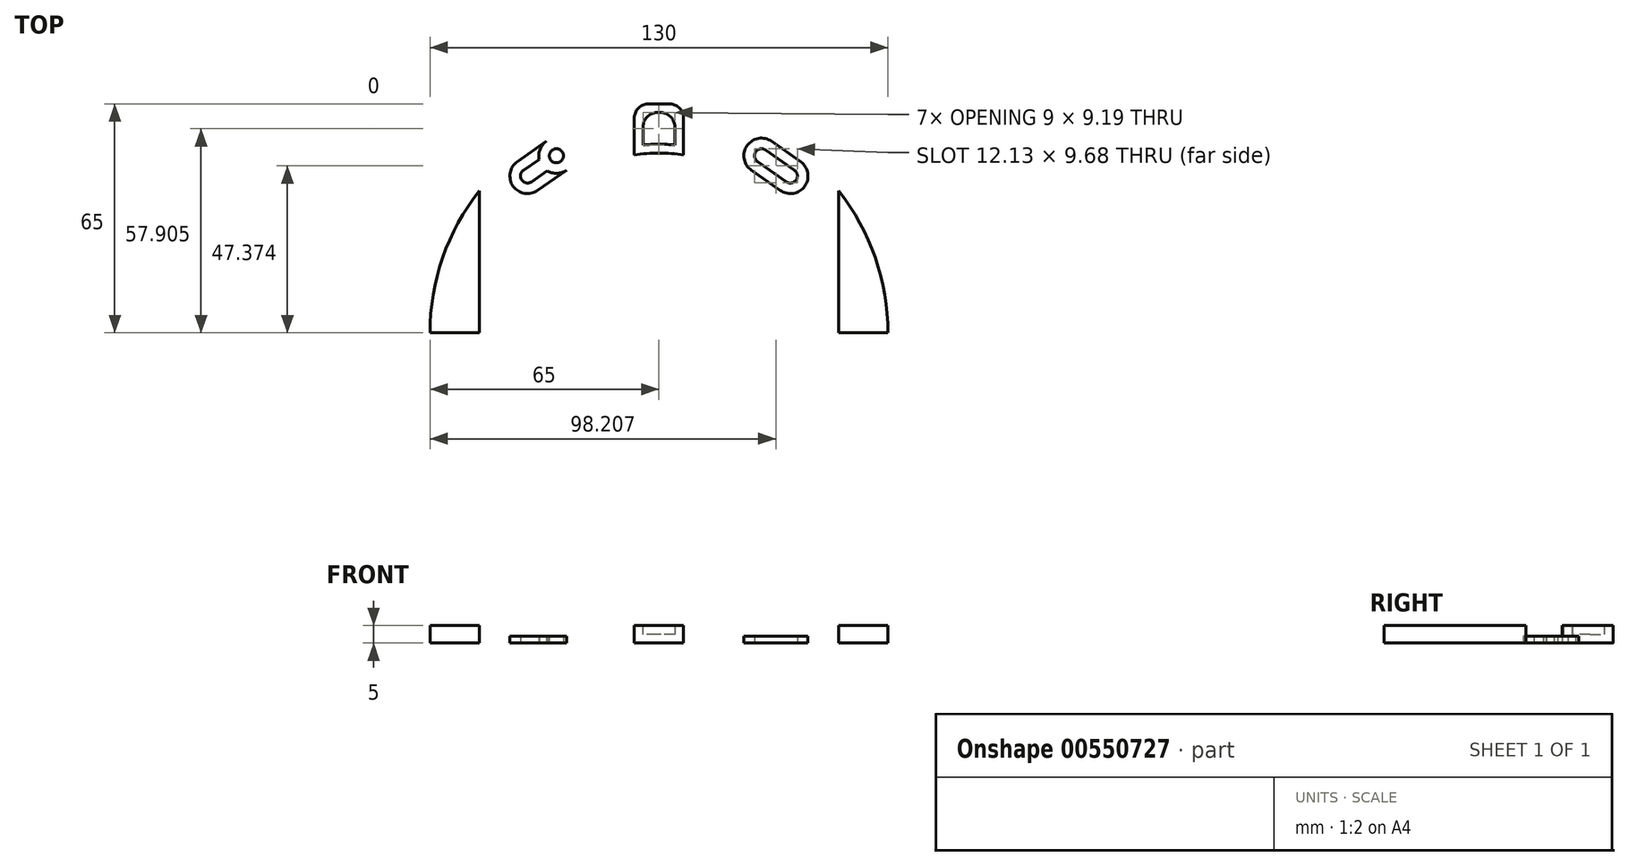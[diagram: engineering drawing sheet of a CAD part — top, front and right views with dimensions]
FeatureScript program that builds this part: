
annotation { "Feature Type Name" : "Feature", "Feature Type Description" : "" }
export const myFeature = defineFeature(function(context is Context, id is Id, definition is map)
    precondition{}
    {
        {
            var Q0;
            Q0=qCreatedBy(makeId("Top.planeOp"),FACE);
            var sketch = newSketch(context, id + "F0", { "sketchPlane" : qUnion([Q0])});
            skLineSegment(sketch, "E0.rect.bottom", {"start": v(-120.25, 41.25) * mm, "end": v(120.25, 41.25) * mm});
            skLineSegment(sketch, "E0.rect.top", {"start": v(-120.25, -41.25) * mm, "end": v(120.25, -41.25) * mm});
            skLineSegment(sketch, "E0.rect.left", {"start": v(-120.25, 41.25) * mm, "end": v(-120.25, -41.25) * mm});
            skLineSegment(sketch, "E0.rect.right", {"start": v(120.25, 41.25) * mm, "end": v(120.25, -41.25) * mm});
            skPoint(sketch, "E0.rect.middle", {"position": v(0, 0) * mm});
            skLineSegment(sketch, "E1.rect.bottom", {"start": v(-65, 41.25) * mm, "end": v(65, 41.25) * mm});
            skLineSegment(sketch, "E1.rect.top", {"start": v(-65, -41.25) * mm, "end": v(65, -41.25) * mm});
            skLineSegment(sketch, "E1.rect.left", {"start": v(-65, 41.25) * mm, "end": v(-65, -41.25) * mm});
            skLineSegment(sketch, "E1.rect.right", {"start": v(65, 41.25) * mm, "end": v(65, -41.25) * mm});
            skArc(sketch, "E2", {"start": v(65, -41.25) * mm, "mid": v(0, 23.75) * mm, "end": v(-65, -41.25) * mm});
            skLineSegment(sketch, "E3.rect.bottom", {"start": v(-51, 41.25) * mm, "end": v(51, 41.25) * mm});
            skLineSegment(sketch, "E3.rect.top", {"start": v(-51, -41.25) * mm, "end": v(51, -41.25) * mm});
            skLineSegment(sketch, "E3.rect.left", {"start": v(-51, 41.25) * mm, "end": v(-51, -41.25) * mm});
            skLineSegment(sketch, "E3.rect.right", {"start": v(51, 41.25) * mm, "end": v(51, -41.25) * mm});
            skArc(sketch, "E4", {"start": v(51, -41.25) * mm, "mid": v(0, 9.75) * mm, "end": v(-51, -41.25) * mm});
            skLineSegment(sketch, "E5.rect.bottom", {"start": v(-7, 41.25) * mm, "end": v(7, 41.25) * mm});
            skLineSegment(sketch, "E5.rect.top", {"start": v(-7, -41.25) * mm, "end": v(7, -41.25) * mm});
            skLineSegment(sketch, "E5.rect.left", {"start": v(-7, 41.25) * mm, "end": v(-7, -41.25) * mm});
            skLineSegment(sketch, "E5.rect.right", {"start": v(7, 41.25) * mm, "end": v(7, -41.25) * mm});
            skLineSegment(sketch, "E6", {"start": v(7, -41.25) * mm, "end": v(51, 41.25) * mm, "construction": true});
            skLineSegment(sketch, "E7", {"start": v(0, -41.25) * mm, "end": v(0, 41.25) * mm, "construction": true});
            skLineSegment(sketch, "E8", {"start": v(29.27, 0.51) * mm, "end": v(19.45, 7.4) * mm, "construction": true});
            skLineSegment(sketch, "E9", {"start": v(35.9, 12.94) * mm, "end": v(27.31, 18.62) * mm, "construction": true});
            skLineSegment(sketch, "E10", {"start": v(19.45, 7.4) * mm, "end": v(27.31, 18.62) * mm, "construction": true});
            skLineSegment(sketch, "E11", {"start": v(29.27, 0.51) * mm, "end": v(39.1, -6.38) * mm, "construction": true});
            skLineSegment(sketch, "E12", {"start": v(39.1, -6.38) * mm, "end": v(46.97, 4.85) * mm, "construction": true});
            skLineSegment(sketch, "E13", {"start": v(19.45, 7.4) * mm, "end": v(46.97, 4.85) * mm, "construction": true});
            skLineSegment(sketch, "E14", {"start": v(27.31, 18.62) * mm, "end": v(39.1, -6.38) * mm, "construction": true});
            skLineSegment(sketch, "E15", {"start": v(35.9, 12.94) * mm, "end": v(46.97, 4.85) * mm, "construction": true});
            skLineSegment(sketch, "E16", {"start": v(43.03, -0.76) * mm, "end": v(23.38, 13.01) * mm, "construction": true});
            skLineSegment(sketch, "E17", {"start": v(33.2, 6.12) * mm, "end": v(29.11, 9) * mm, "construction": true});
            skLineSegment(sketch, "E18", {"start": v(33.2, 6.12) * mm, "end": v(37.3, 3.25) * mm, "construction": true});
            skLineSegment(sketch, "E19", {"start": v(37.3, 3.25) * mm, "end": v(38.45, 4.9) * mm});
            skLineSegment(sketch, "E20", {"start": v(29.11, 9) * mm, "end": v(30.26, 10.63) * mm});
            skLineSegment(sketch, "E21", {"start": v(30.26, 10.63) * mm, "end": v(38.45, 4.9) * mm});
            skLineSegment(sketch, "E22", {"start": v(37.3, 3.25) * mm, "end": v(36.15, 1.62) * mm});
            skLineSegment(sketch, "E23", {"start": v(29.11, 9) * mm, "end": v(27.96, 7.36) * mm});
            skLineSegment(sketch, "E24", {"start": v(27.96, 7.36) * mm, "end": v(36.15, 1.62) * mm});
            skLineSegment(sketch, "E25", {"start": v(37.3, 3.25) * mm, "end": v(40.17, 7.35) * mm});
            skLineSegment(sketch, "E26", {"start": v(29.11, 9) * mm, "end": v(31.98, 13.09) * mm});
            skLineSegment(sketch, "E27", {"start": v(29.11, 9) * mm, "end": v(26.24, 4.9) * mm});
            skLineSegment(sketch, "E28", {"start": v(37.3, 3.25) * mm, "end": v(34.43, -0.84) * mm});
            skLineSegment(sketch, "E29", {"start": v(31.98, 13.09) * mm, "end": v(40.17, 7.35) * mm});
            skLineSegment(sketch, "E30", {"start": v(34.43, -0.84) * mm, "end": v(26.24, 4.9) * mm});
            skCircle(sketch, "E31", {"center": v(37.3, 3.25) * mm, "radius": 2 * mm});
            skCircle(sketch, "E32", {"center": v(29.11, 9) * mm, "radius": 2 * mm});
            skCircle(sketch, "E33", {"center": v(29.11, 9) * mm, "radius": 5 * mm});
            skCircle(sketch, "E34", {"center": v(37.3, 3.25) * mm, "radius": 5 * mm});
            skLineSegment(sketch, "E35.0.MirrorCS", {"start": v(-34.43, -0.84) * mm, "end": v(-26.24, 4.9) * mm});
            skCircle(sketch, "E35.1.MirrorC", {"center": v(-29.11, 9) * mm, "radius": 2 * mm});
            skLineSegment(sketch, "E35.2.MirrorCS", {"start": v(-27.96, 7.36) * mm, "end": v(-36.15, 1.62) * mm});
            skCircle(sketch, "E35.3.MirrorC", {"center": v(-37.3, 3.25) * mm, "radius": 2 * mm});
            skLineSegment(sketch, "E35.4.MirrorCS", {"start": v(-30.26, 10.63) * mm, "end": v(-38.45, 4.9) * mm});
            skLineSegment(sketch, "E35.5.MirrorCS", {"start": v(-31.98, 13.09) * mm, "end": v(-40.17, 7.35) * mm});
            skCircle(sketch, "E35.6.MirrorC", {"center": v(-29.11, 9) * mm, "radius": 5 * mm});
            skCircle(sketch, "E35.7.MirrorC", {"center": v(-37.3, 3.25) * mm, "radius": 5 * mm});
            skLineSegment(sketch, "E36.top", {"start": v(-51, -19.25) * mm, "end": v(51, -19.25) * mm});
            skLineSegment(sketch, "E36.left", {"start": v(-51, -41.25) * mm, "end": v(-51, -19.25) * mm});
            skLineSegment(sketch, "E36.right", {"start": v(51, -41.25) * mm, "end": v(51, -19.25) * mm});
            skLineSegment(sketch, "E37", {"start": v(-120.25, 0) * mm, "end": v(120.25, -0.84) * mm, "construction": true});
            skLineSegment(sketch, "E38", {"start": v(65, -41.25) * mm, "end": v(65, 41.25) * mm, "construction": true});
            skSolve(sketch);
        }
        {
            var Q0;
            {var subQ2=sQuery(id+"F0.wireOp",EDGE,"E35.0.MirrorCS");Q0=makeQuery(id+"F0.imprint","IMPRINT",FACE,{"disambiguationData":[TD([[makeQuery(id+"F0.imprint","IMPRINT",EDGE,{"derivedFrom":subQ2}),-1.0]])]});}
            var Q1;
            {var subQ0=sQuery(id+"F0.wireOp",EDGE,"E2");var subQ1=sQuery(id+"F0.wireOp",EDGE,"E3.rect.left");var subQ2=makeQuery(id+"F0.imprint","INTERSECT",VERTEX,{"derivedFrom":[subQ0,subQ1]});Q1=makeQuery(id+"F0.imprint","IMPRINT",FACE,{"disambiguationData":[TD([[makeQuery(id+"F0.imprint","IMPRINT",EDGE,{"disambiguationData":[TD([[subQ2,-1.0]])],"derivedFrom":subQ0}),1.0]])]});}
            var Q2;
            {var subQ0=sQuery(id+"F0.wireOp",EDGE,"E5.rect.right");var subQ3=sQuery(id+"F0.wireOp",EDGE,"E2");var subQ4=makeQuery(id+"F0.imprint","INTERSECT",VERTEX,{"derivedFrom":[subQ3,subQ0]});Q2=makeQuery(id+"F0.imprint","IMPRINT",FACE,{"disambiguationData":[TD([[makeQuery(id+"F0.imprint","IMPRINT",EDGE,{"disambiguationData":[TD([[subQ4,-1.0]])],"derivedFrom":subQ3}),1.0]])]});}
            var Q3;
            {var subQ2=sQuery(id+"F0.wireOp",EDGE,"E29");Q3=makeQuery(id+"F0.imprint","IMPRINT",FACE,{"disambiguationData":[TD([[makeQuery(id+"F0.imprint","IMPRINT",EDGE,{"derivedFrom":subQ2}),1.0]])]});}
            var Q4;
            {var subQ0=sQuery(id+"F0.wireOp",EDGE,"E3.rect.right");var subQ1=sQuery(id+"F0.wireOp",EDGE,"E2");var subQ2=makeQuery(id+"F0.imprint","INTERSECT",VERTEX,{"derivedFrom":[subQ1,subQ0]});Q4=makeQuery(id+"F0.imprint","IMPRINT",FACE,{"disambiguationData":[TD([[makeQuery(id+"F0.imprint","IMPRINT",EDGE,{"disambiguationData":[TD([[subQ2,1.0]])],"derivedFrom":subQ1}),1.0]])]});}
            var Q5;
            {var subQ4=sQuery(id+"F0.wireOp",EDGE,"E5.rect.bottom");Q5=makeQuery(id+"F0.imprint","IMPRINT",FACE,{"disambiguationData":[TD([[makeQuery(id+"F0.imprint","IMPRINT",EDGE,{"derivedFrom":subQ4}),-1.0]])]});}
            var Q6;
            {var subQ0=sQuery(id+"F0.wireOp",EDGE,"a0aa5b6b-2d28-4dbe-b29c-96da90adcfeb");var subQ3=sQuery(id+"F0.wireOp",EDGE,"E1.rect.left");var subQ4=makeQuery(id+"F0.imprint","INTERSECT",VERTEX,{"derivedFrom":[subQ3,subQ0]});Q6=makeQuery(id+"F0.imprint","IMPRINT",FACE,{"disambiguationData":[TD([[makeQuery(id+"F0.imprint","IMPRINT",EDGE,{"disambiguationData":[TD([[subQ4,1.0]])],"derivedFrom":subQ0}),1.0]])]});}
            var Q7;
            {var subQ3=sQuery(id+"F0.wireOp",EDGE,"E36.left");Q7=makeQuery(id+"F0.imprint","IMPRINT",FACE,{"disambiguationData":[TD([[makeQuery(id+"F0.imprint","IMPRINT",EDGE,{"derivedFrom":subQ3}),1.0]])]});}
            var Q8;
            {var subQ3=sQuery(id+"F0.wireOp",EDGE,"E36.right");Q8=makeQuery(id+"F0.imprint","IMPRINT",FACE,{"disambiguationData":[TD([[makeQuery(id+"F0.imprint","IMPRINT",EDGE,{"derivedFrom":subQ3}),-1.0]])]});}
            var Q9;
            {var subQ0=sQuery(id+"F0.wireOp",EDGE,"538e6529-4a32-4181-8bd5-1c901203cef8");var subQ3=sQuery(id+"F0.wireOp",EDGE,"E1.rect.right");var subQ4=makeQuery(id+"F0.imprint","INTERSECT",VERTEX,{"derivedFrom":[subQ3,subQ0]});Q9=makeQuery(id+"F0.imprint","IMPRINT",FACE,{"disambiguationData":[TD([[makeQuery(id+"F0.imprint","IMPRINT",EDGE,{"disambiguationData":[TD([[subQ4,1.0]])],"derivedFrom":subQ0}),-1.0]])]});}
            extrude(context, id + "F1", {"entities" : qUnion([Q0, Q1, Q2, Q3, Q4, Q5, Q6, Q7, Q8, Q9]), "depth" : 5 * mm});
        }
        {
            var Q0;
            {var subQ1=sQuery(id+"F0.wireOp",EDGE,"E35.2.MirrorCS");var subQ7=sQuery(id+"F0.wireOp",EDGE,"E35.3.MirrorC");var subQ9=makeQuery(id+"F0.imprint","INTERSECT",VERTEX,{"derivedFrom":[subQ1,subQ7]});Q0=makeQuery(id+"F0.imprint","IMPRINT",FACE,{"disambiguationData":[TD([[makeQuery(id+"F0.imprint","IMPRINT",EDGE,{"disambiguationData":[TD([[subQ9,1.0]])],"derivedFrom":subQ1}),1.0]])]});}
            var Q1;
            {var subQ4=sQuery(id+"F0.wireOp",EDGE,"E35.2.MirrorCS");var subQ7=sQuery(id+"F0.wireOp",EDGE,"E35.1.MirrorC");var subQ9=makeQuery(id+"F0.imprint","INTERSECT",VERTEX,{"derivedFrom":[subQ7,subQ4]});Q1=makeQuery(id+"F0.imprint","IMPRINT",FACE,{"disambiguationData":[TD([[makeQuery(id+"F0.imprint","IMPRINT",EDGE,{"disambiguationData":[TD([[subQ9,1.0]])],"derivedFrom":subQ7}),1.0]])]});}
            var Q2;
            {var subQ3=sQuery(id+"F0.wireOp",EDGE,"E35.0.MirrorCS");Q2=makeQuery(id+"F0.imprint","IMPRINT",FACE,{"disambiguationData":[TD([[makeQuery(id+"F0.imprint","IMPRINT",EDGE,{"derivedFrom":subQ3}),1.0]])]});}
            var Q3;
            {var subQ3=sQuery(id+"F0.wireOp",EDGE,"E35.5.MirrorCS");Q3=makeQuery(id+"F0.imprint","IMPRINT",FACE,{"disambiguationData":[TD([[makeQuery(id+"F0.imprint","IMPRINT",EDGE,{"derivedFrom":subQ3}),1.0]])]});}
            var Q4;
            {var subQ3=sQuery(id+"F0.wireOp",EDGE,"E29");Q4=makeQuery(id+"F0.imprint","IMPRINT",FACE,{"disambiguationData":[TD([[makeQuery(id+"F0.imprint","IMPRINT",EDGE,{"derivedFrom":subQ3}),-1.0]])]});}
            var Q5;
            {var subQ0=sQuery(id+"F0.wireOp",EDGE,"E33");var subQ1=sQuery(id+"F0.wireOp",EDGE,"E21");var subQ2=makeQuery(id+"F0.imprint","INTERSECT",VERTEX,{"derivedFrom":[subQ1,subQ0]});Q5=makeQuery(id+"F0.imprint","IMPRINT",FACE,{"disambiguationData":[TD([[makeQuery(id+"F0.imprint","IMPRINT",EDGE,{"disambiguationData":[TD([[subQ2,1.0]])],"derivedFrom":subQ1}),1.0]])]});}
            var Q6;
            {var subQ3=sQuery(id+"F0.wireOp",EDGE,"E26");var subQ5=sQuery(id+"F0.wireOp",EDGE,"E32");var subQ7=makeQuery(id+"F0.imprint","INTERSECT",VERTEX,{"derivedFrom":[sQuery(id+"F0.wireOp",EDGE,"E21"),subQ3,subQ5]});Q6=makeQuery(id+"F0.imprint","IMPRINT",FACE,{"disambiguationData":[TD([[makeQuery(id+"F0.imprint","IMPRINT",EDGE,{"disambiguationData":[TD([[subQ7,-1.0]])],"derivedFrom":subQ3}),1.0]])]});}
            var Q7;
            {var subQ1=sQuery(id+"F0.wireOp",EDGE,"E33");var subQ3=sQuery(id+"F0.wireOp",EDGE,"E24");var subQ5=makeQuery(id+"F0.imprint","INTERSECT",VERTEX,{"derivedFrom":[subQ3,subQ1]});Q7=makeQuery(id+"F0.imprint","IMPRINT",FACE,{"disambiguationData":[TD([[makeQuery(id+"F0.imprint","IMPRINT",EDGE,{"disambiguationData":[TD([[subQ5,1.0]])],"derivedFrom":subQ3}),-1.0]])]});}
            var Q8;
            {var subQ3=sQuery(id+"F0.wireOp",EDGE,"E30");Q8=makeQuery(id+"F0.imprint","IMPRINT",FACE,{"disambiguationData":[TD([[makeQuery(id+"F0.imprint","IMPRINT",EDGE,{"derivedFrom":subQ3}),-1.0]])]});}
            var Q9;
            {var subQ1=sQuery(id+"F0.wireOp",EDGE,"E34");var subQ3=sQuery(id+"F0.wireOp",EDGE,"E24");var subQ5=makeQuery(id+"F0.imprint","INTERSECT",VERTEX,{"derivedFrom":[subQ3,subQ1]});Q9=makeQuery(id+"F0.imprint","IMPRINT",FACE,{"disambiguationData":[TD([[makeQuery(id+"F0.imprint","IMPRINT",EDGE,{"disambiguationData":[TD([[subQ5,-1.0]])],"derivedFrom":subQ3}),-1.0]])]});}
            var Q10;
            {var subQ3=sQuery(id+"F0.wireOp",EDGE,"E25");var subQ5=sQuery(id+"F0.wireOp",EDGE,"E31");var subQ7=makeQuery(id+"F0.imprint","INTERSECT",VERTEX,{"derivedFrom":[sQuery(id+"F0.wireOp",EDGE,"E21"),subQ3,subQ5]});Q10=makeQuery(id+"F0.imprint","IMPRINT",FACE,{"disambiguationData":[TD([[makeQuery(id+"F0.imprint","IMPRINT",EDGE,{"disambiguationData":[TD([[subQ7,-1.0]])],"derivedFrom":subQ3}),-1.0]])]});}
            var Q11;
            {var subQ0=sQuery(id+"F0.wireOp",EDGE,"E34");var subQ1=sQuery(id+"F0.wireOp",EDGE,"E21");var subQ2=makeQuery(id+"F0.imprint","INTERSECT",VERTEX,{"derivedFrom":[subQ1,subQ0]});Q11=makeQuery(id+"F0.imprint","IMPRINT",FACE,{"disambiguationData":[TD([[makeQuery(id+"F0.imprint","IMPRINT",EDGE,{"disambiguationData":[TD([[subQ2,-1.0]])],"derivedFrom":subQ1}),1.0]])]});}
            extrude(context, id + "F2", {"entities" : qUnion([Q0, Q1, Q2, Q3, Q4, Q5, Q6, Q7, Q8, Q9, Q10, Q11]), "operationType" : NewBodyOperationType.ADD, "depth" : 2 * mm});
        }
        {
            var Q0;
            Q0=makeQuery(id+"F1.opExtrude","CAP_FACE",FACE,{"disambiguationData":[OSD([sQuery(id+"F0.wireOp",EDGE,"E1.rect.top"),sQuery(id+"F0.wireOp",EDGE,"E2"),sQuery(id+"F0.wireOp",EDGE,"E4"),sQuery(id+"F0.wireOp",EDGE,"E5.rect.bottom"),sQuery(id+"F0.wireOp",EDGE,"E5.rect.left"),sQuery(id+"F0.wireOp",EDGE,"E5.rect.right"),sQuery(id+"F0.wireOp",EDGE,"E29"),sQuery(id+"F0.wireOp",EDGE,"E30"),sQuery(id+"F0.wireOp",EDGE,"E33"),sQuery(id+"F0.wireOp",EDGE,"E34"),sQuery(id+"F0.wireOp",EDGE,"E35.0.MirrorCS"),sQuery(id+"F0.wireOp",EDGE,"E35.5.MirrorCS"),sQuery(id+"F0.wireOp",EDGE,"E35.6.MirrorC"),sQuery(id+"F0.wireOp",EDGE,"E35.7.MirrorC")])],"isStart":false});
            shell(context, id + "F3", {"entities" : qUnion([Q0]), "thickness" : 2.5 * mm});
        }
        {
            var Q0;
            Q0=makeQuery(id+"F1.opExtrude","SWEPT_EDGE",EDGE,{"disambiguationData":[OSD([sQuery(id+"F0.wireOp",EDGE,"E2"),sQuery(id+"F0.wireOp",EDGE,"E5.rect.left")])]});
            var Q1;
            Q1=makeQuery(id+"F1.opExtrude","SWEPT_EDGE",EDGE,{"disambiguationData":[OSD([sQuery(id+"F0.wireOp",EDGE,"E2"),sQuery(id+"F0.wireOp",EDGE,"E5.rect.right")])]});
            var Q2;
            Q2=makeQuery(id+"F3.opShell","OFFSET_EDGE",EDGE,{"disambiguationData":[OSD([sQuery(id+"F0.wireOp",EDGE,"E2"),sQuery(id+"F0.wireOp",EDGE,"E5.rect.left")])]});
            var Q3;
            Q3=makeQuery(id+"F3.opShell","OFFSET_EDGE",EDGE,{"disambiguationData":[OSD([sQuery(id+"F0.wireOp",EDGE,"E2"),sQuery(id+"F0.wireOp",EDGE,"E5.rect.right")])]});
            fillet(context, id + "F4", {"entities" : qUnion([Q0, Q1, Q2, Q3]), "radius" : 4 * mm, "tangentPropagation" : true, "allowEdgeOverflow" : false});
        }
    });
